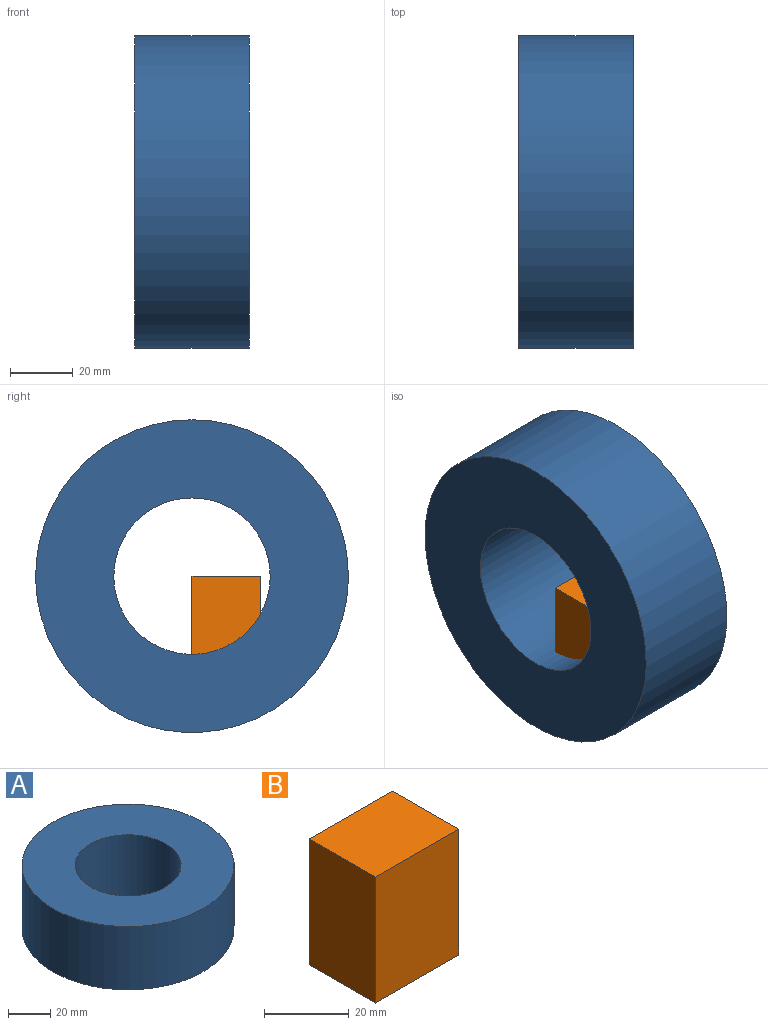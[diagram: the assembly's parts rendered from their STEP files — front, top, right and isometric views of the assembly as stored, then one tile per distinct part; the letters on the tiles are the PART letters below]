
ASSEMBLY  parts=2 mates=1
PART A: 4 faces, bbox 100x100x36.5 mm
  f0: cylinder r=25mm len=50mm, axis (0,0,-1), area 5733.4mm2, adj f2,f3
  f1: cylinder r=50mm len=100mm, axis (0,0,-1), area 11466.8mm2, adj f2,f3
  f2: plane 100x100mm, normal (0,0,1), area 5890.5mm2, adj f0,f1
  f3: plane 100x100mm, normal (0,0,-1), area 5890.5mm2, adj f0,f1
PART B: 6 faces, bbox 27.7x22x36.3 mm
  f0: plane 36.3x21.99mm, normal (-1,0,0), area 798.3mm2, adj f1,f3,f4,f5
  f1: plane 36.3x27.66mm, normal (0,-1,0), area 1004mm2, adj f0,f2,f4,f5
  f2: plane 36.3x21.99mm, normal (1,0,0), area 798.3mm2, adj f1,f3,f4,f5
  f3: plane 36.3x27.66mm, normal (0,1,0), area 1004mm2, adj f0,f2,f4,f5
  f4: plane 27.66x21.99mm, normal (0,0,1), area 608.3mm2, adj f0,f1,f2,f3
  f5: plane 27.66x21.99mm, normal (0,0,-1), area 608.3mm2, adj f0,f1,f2,f3
PLACE A rot(axis=(0,-1,0),90deg) t=(0.39,-20.26,65.09)mm
PLACE B rot(axis=(1,0,0),180deg) t=(-56.55,-111.13,30)mm
MATE fastened B.f2 <-> A.f0  axis (1,0,0) through (0.39,-55.56,30)mm
